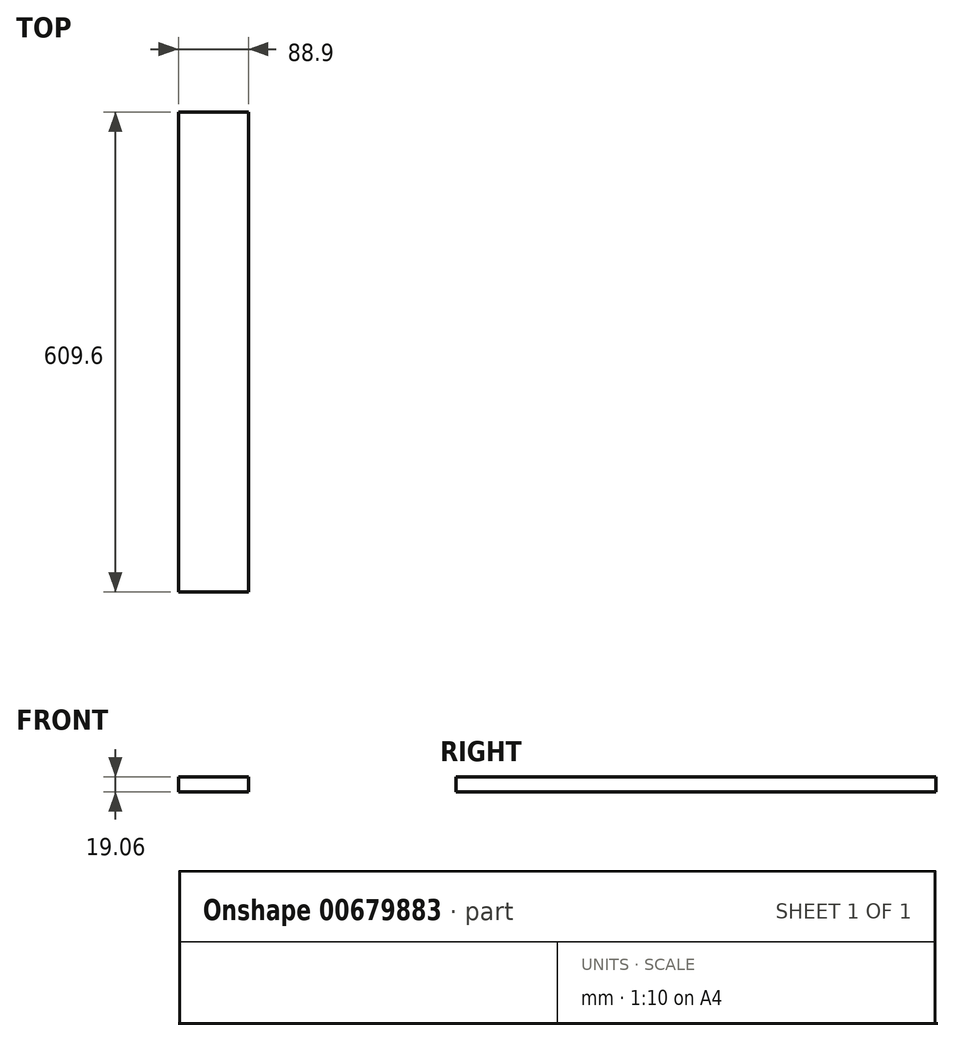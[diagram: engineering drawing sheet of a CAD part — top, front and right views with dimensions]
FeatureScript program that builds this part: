
annotation { "Feature Type Name" : "Feature", "Feature Type Description" : "" }
export const myFeature = defineFeature(function(context is Context, id is Id, definition is map)
    precondition{}
    {
        {
            var Q0;
            Q0=qCreatedBy(makeId("Front.planeOp"),FACE);
            var sketch = newSketch(context, id + "F0", { "sketchPlane" : qUnion([Q0])});
            skLineSegment(sketch, "E0.bottom", {"start": v(44.45, 9.53) * mm, "end": v(-44.45, 9.53) * mm});
            skLineSegment(sketch, "E0.top", {"start": v(44.45, -9.53) * mm, "end": v(-44.45, -9.53) * mm});
            skLineSegment(sketch, "E0.left", {"start": v(44.45, 9.53) * mm, "end": v(44.45, -9.53) * mm});
            skLineSegment(sketch, "E0.right", {"start": v(-44.45, 9.53) * mm, "end": v(-44.45, -9.53) * mm});
            skPoint(sketch, "E0.middle", {"position": v(0, 0) * mm});
            skSolve(sketch);
        }
        {
            var Q0;
            Q0=makeQuery(id+"F0.imprint","IMPRINT",FACE,{"disambiguationData":[TD([[makeQuery(id+"F0.imprint","IMPRINT",EDGE,{"derivedFrom":sQuery(id+"F0.wireOp",EDGE,"E0.bottom")}),1.0]])]});
            extrude(context, id + "F1", {"entities" : qUnion([Q0]), "endBound" : BoundingType.SYMMETRIC, "depth" : 609.6 * mm, "offsetDistance" : 25.4 * mm});
        }
    });
